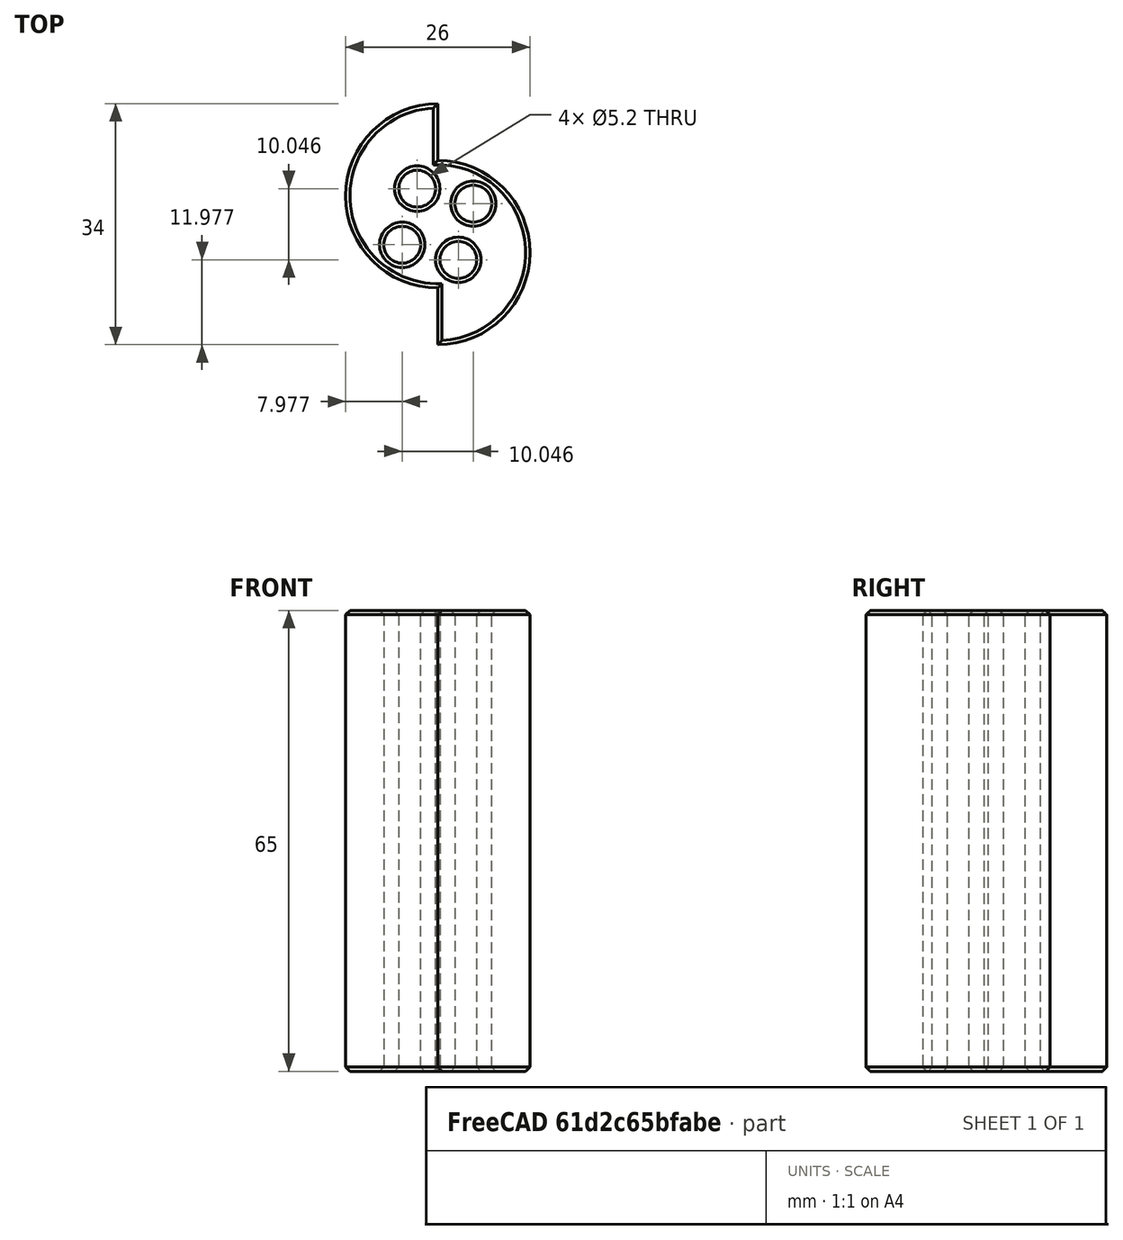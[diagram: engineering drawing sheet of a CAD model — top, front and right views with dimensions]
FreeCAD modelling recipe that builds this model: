
FCSTD DOCUMENT  (FreeCAD 0.18R4 (GitTag))
Label: Wheel
License: All rights reserved
LicenseURL: http://en.wikipedia.org/wiki/All_rights_reserved
objects: Sketcher::SketchObject×3, PartDesign::Pocket×2, PartDesign::Revolution×1, PartDesign::PolarPattern×1, PartDesign::Chamfer×1, PartDesign::Body×1, Mesh::Feature×1
note: 12 computed .brp shape members not serialized (recipe doc carries the construction recipe); baked Part::Feature solids carry a one-line shape summary decoded from their .brp

FEATURE [Sketcher::SketchObject] Sketch
  MapMode = 5
  Placement = pos=(0,0,0) rot=(1,0,0;1.5708rad)
  Support = -> [XZ_Plane]
  sketch-geometry (4):
    g0: LineSegment StartX=0 StartY=0 StartZ=0 EndX=17 EndY=0 EndZ=0
    g1: LineSegment StartX=17 StartY=0 StartZ=0 EndX=17 EndY=65 EndZ=0
    g2: LineSegment StartX=17 StartY=65 StartZ=0 EndX=0 EndY=65 EndZ=0
    g3: LineSegment StartX=0 StartY=65 StartZ=0 EndX=0 EndY=0 EndZ=0
  constraints (11):
    c: Coincident(g-1,g0)
    c: PointOnObject(g0,g-1)
    c: Coincident(g0,g1)
    c: Vertical(g1)
    c: Coincident(g1,g2)
    c: Horizontal(g2)
    c: PointOnObject(g3,g-2)
    c: DistanceX(g0,g0) = 17
    c: DistanceY(g1,g1) = 65
    c: Coincident(g3,g0)
    c: Coincident(g2,g3)
FEATURE [PartDesign::Revolution] Revolution
  Angle = 360
  Axis = (0,-2e-16,1)
  Base = (0,0,0)
  Placement = pos=(0,0,0) rot=(1,0,0;1.5708rad)
  Profile = -> Sketch
  ReferenceAxis = -> Sketch [V_Axis]
  Refine = true
  Reversed = true
FEATURE [Sketcher::SketchObject] Sketch001
  ExternalGeometry = -> [Revolution]
  MapMode = 5
  Placement = pos=(0,-1.44e-14,65) rot=(0,0,1;3.14159rad)
  Support = -> [Revolution]
  sketch-geometry (5):
    g0: LineSegment StartX=0 StartY=17 StartZ=0 EndX=17 EndY=17 EndZ=0
    g1: LineSegment StartX=0 StartY=17 StartZ=0 EndX=8.6175e-12 EndY=9 EndZ=0
    g2: ArcOfCircle CenterX=0 CenterY=-4 CenterZ=0 NormalX=0 NormalY=0 NormalZ=1 AngleXU=0 Radius=13 StartAngle=4.71239 EndAngle=7.85398
    g3: LineSegment StartX=17 StartY=17 StartZ=0 EndX=17 EndY=-17 EndZ=0
    g4: LineSegment StartX=17 StartY=-17 StartZ=0 EndX=9.3507e-12 EndY=-17 EndZ=0
  constraints (16):
    c: PointOnObject(g0,g-2)
    c: Horizontal(g0)
    c: Coincident(g1,g0)
    c: PointOnObject(g1,g-2)
    c: Coincident(g2,g1)
    c: PointOnObject(g0,g-3)
    c: PointOnObject(g2,g-3)
    c: PointOnObject(g2,g-2)
    c: DistanceY(g1,g1) = 8
    c: Coincident(g0,g3)
    c: Vertical(g3)
    c: Coincident(g3,g4)
    c: Coincident(g4,g2)
    c: Horizontal(g4)
    c: Tangent(g3,g-3)
    c: PointOnObject(g2,g-2)
FEATURE [PartDesign::Pocket] Pocket
  BaseFeature = -> Revolution
  Length = 65
  Length2 = 100
  Placement = pos=(0,0,0) rot=(1,0,0;1.5708rad)
  Profile = -> Sketch001
  Refine = true
  Type = 0
FEATURE [PartDesign::PolarPattern] PolarPattern
  Angle = 360
  Axis = -> Sketch001 [N_Axis]
  BaseFeature = -> Pocket
  Occurrences = 2
  Originals = -> [Pocket]
  Placement = pos=(0,0,0) rot=(1,0,0;1.5708rad)
  Refine = true
FEATURE [Sketcher::SketchObject] Sketch002
  MapMode = 5
  Placement = pos=(0,-1.44e-14,65) rot=(0,0,1;3.14159rad)
  Support = -> [PolarPattern]
  sketch-geometry (7):
    g0: Circle [constr] CenterX=0 CenterY=0 CenterZ=0 NormalX=0 NormalY=0 NormalZ=1 AngleXU=0 Radius=5.8
    g1: Circle CenterX=-2.9 CenterY=5.02295 CenterZ=0 NormalX=0 NormalY=0 NormalZ=1 AngleXU=0 Radius=2.6
    g2: Circle CenterX=2.9 CenterY=-5.02295 CenterZ=0 NormalX=0 NormalY=0 NormalZ=1 AngleXU=0 Radius=2.6
    g3: LineSegment [constr] StartX=-2.9 StartY=5.02295 StartZ=0 EndX=2.9 EndY=-5.02295 EndZ=0
    g4: LineSegment [constr] StartX=-5.02295 StartY=-2.9 StartZ=0 EndX=5.02295 EndY=2.9 EndZ=0
    g5: Circle CenterX=5.02295 CenterY=2.9 CenterZ=0 NormalX=0 NormalY=0 NormalZ=1 AngleXU=0 Radius=2.6
    g6: Circle CenterX=-5.02295 CenterY=-2.9 CenterZ=0 NormalX=0 NormalY=0 NormalZ=1 AngleXU=0 Radius=2.6
  constraints (18):
    c: Radius(g0) = 5.8
    c: PointOnObject(g1,g0)
    c: PointOnObject(g2,g0)
    c: Radius(g2) = 2.6
    c: Radius(g1) = 2.6
    c: Coincident(g3,g1)
    c: Coincident(g3,g2)
    c: Angle(g-2,g3) = 0.523599
    c: PointOnObject(g4,g0)
    c: PointOnObject(g4,g0)
    c: Coincident(g0,g-1)
    c: PointOnObject(g-1,g3)
    c: PointOnObject(g-1,g4)
    c: Angle(g3,g4) = 1.5708
    c: Coincident(g5,g4)
    c: Coincident(g6,g4)
    c: Equal(g5,g6)
    c: Equal(g6,g2)
FEATURE [PartDesign::Pocket] Pocket001
  BaseFeature = -> PolarPattern
  Length = 65
  Length2 = 100
  Placement = pos=(0,0,0) rot=(1,0,0;1.5708rad)
  Profile = -> Sketch002
  Refine = true
  Type = 0
FEATURE [PartDesign::Chamfer] Chamfer
  Base = -> Pocket001 [Face10,Face1]
  BaseFeature = -> Pocket001
  Placement = pos=(0,0,0) rot=(1,0,0;1.5708rad)
  Size = 0.6
FEATURE [PartDesign::Body] Body
  Group = -> [Sketch,Revolution,Sketch001,Pocket,PolarPattern,Sketch002,Pocket001,Chamfer]
  Origin = -> Origin
  Tip = -> Chamfer
FEATURE [Mesh::Feature] Mesh  label="Chamfer (Meshed)"
